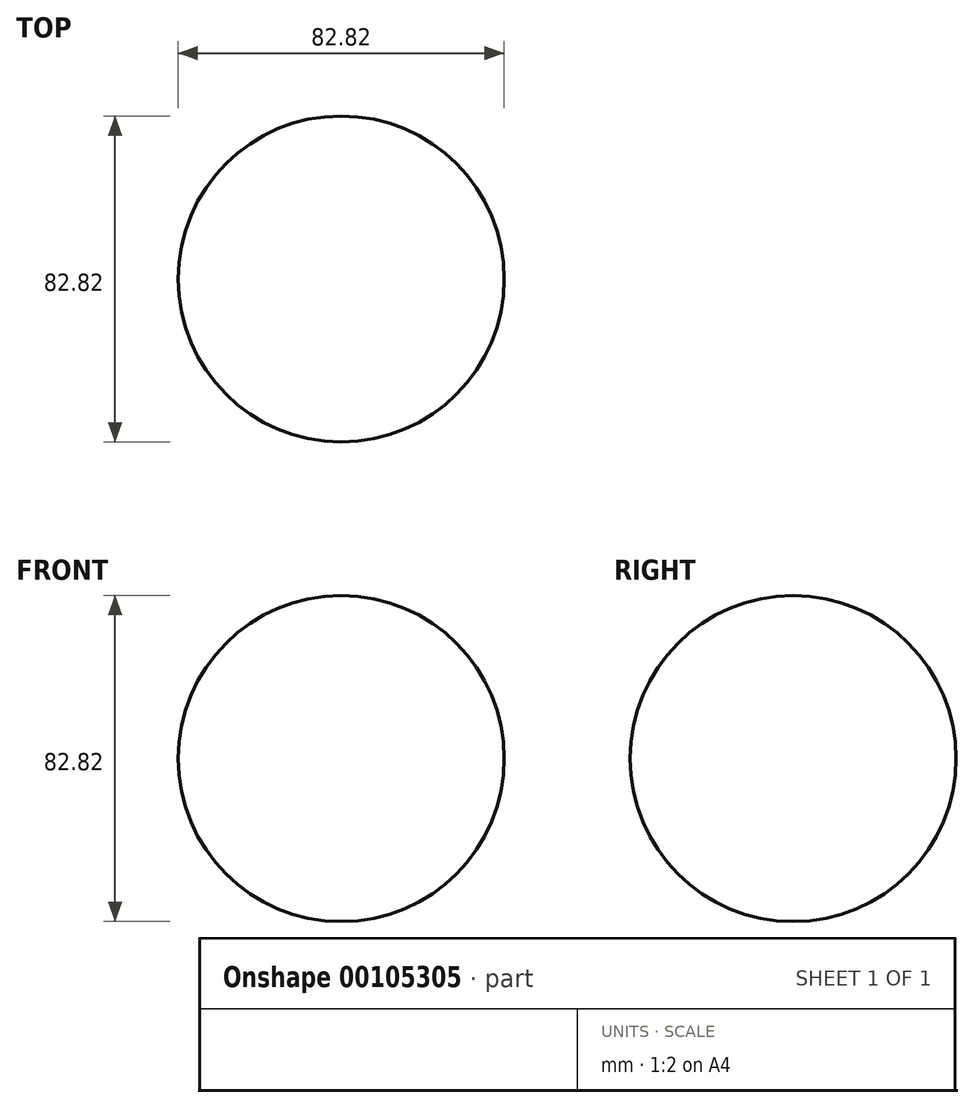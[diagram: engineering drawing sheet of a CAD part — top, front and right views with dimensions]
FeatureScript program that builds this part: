
annotation { "Feature Type Name" : "Feature", "Feature Type Description" : "" }
export const myFeature = defineFeature(function(context is Context, id is Id, definition is map)
    precondition{}
    {
        {
            var Q0;
            Q0=qCreatedBy(makeId("Front.planeOp"),FACE);
            var sketch = newSketch(context, id + "F0", { "sketchPlane" : qUnion([Q0])});
            skArc(sketch, "E0", {"start": v(0, 22.36) * mm, "mid": v(-41.41, -19.05) * mm, "end": v(0, -60.46) * mm});
            skLineSegment(sketch, "E1", {"start": v(0, 22.36) * mm, "end": v(0, -60.46) * mm});
            skSolve(sketch);
        }
        {
            var Q0;
            Q0=makeQuery(id+"F0.imprint","IMPRINT",FACE,{"disambiguationData":[TD([[makeQuery(id+"F0.imprint","IMPRINT",EDGE,{"derivedFrom":sQuery(id+"F0.wireOp",EDGE,"E0")}),1.0]])]});
            var Q1;
            Q1=sQuery(id+"F0.wireOp",EDGE,"E1");
            revolve(context, id + "F1", {"entities" : qUnion([Q0]), "axis" : qUnion([Q1]), "revolveType" : RevolveType.FULL});
        }
    });
